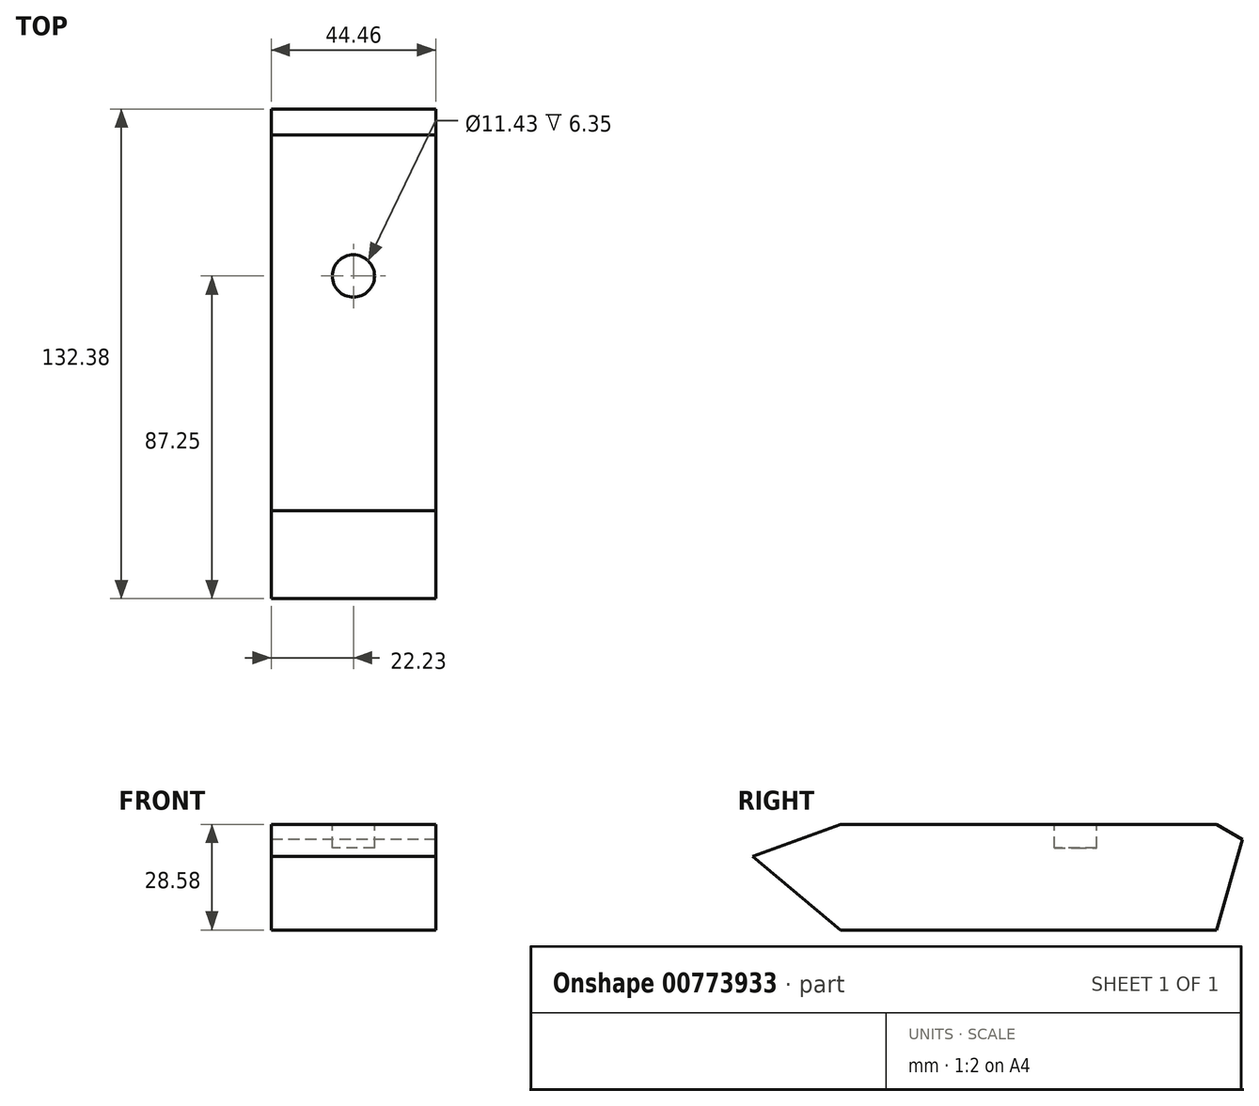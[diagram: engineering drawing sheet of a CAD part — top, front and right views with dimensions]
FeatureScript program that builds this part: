
annotation { "Feature Type Name" : "Feature", "Feature Type Description" : "" }
export const myFeature = defineFeature(function(context is Context, id is Id, definition is map)
    precondition{}
    {
        {
            var Q0;
            Q0=qCreatedBy(makeId("Right.planeOp"),FACE);
            var sketch = newSketch(context, id + "F0", { "sketchPlane" : qUnion([Q0])});
            skLineSegment(sketch, "E0.bottom", {"start": v(-50.8, 14.29) * mm, "end": v(50.8, 14.29) * mm});
            skLineSegment(sketch, "E0.top", {"start": v(-50.8, -14.29) * mm, "end": v(50.8, -14.29) * mm});
            skLineSegment(sketch, "E0.left", {"start": v(-50.8, 14.29) * mm, "end": v(-50.8, -14.29) * mm});
            skLineSegment(sketch, "E0.right", {"start": v(50.8, 14.29) * mm, "end": v(50.8, -14.29) * mm});
            skPoint(sketch, "E0.middle", {"position": v(0, 0) * mm});
            skLineSegment(sketch, "E1", {"start": v(-50.8, 14.29) * mm, "end": v(-74.55, 5.64) * mm});
            skLineSegment(sketch, "E2", {"start": v(-74.55, 5.64) * mm, "end": v(-50.8, -14.29) * mm});
            skLineSegment(sketch, "E3", {"start": v(50.8, 14.29) * mm, "end": v(57.83, 10.23) * mm});
            skLineSegment(sketch, "E4", {"start": v(50.8, -14.29) * mm, "end": v(57.83, 10.23) * mm});
            skSolve(sketch);
        }
        {
            var Q0;
            Q0 = qSketchRegion(id + "F0", true);
            extrude(context, id + "F1", {"entities" : qUnion([Q0]), "endBound" : BoundingType.SYMMETRIC, "depth" : 44.45 * mm, "offsetDistance" : 25.4 * mm});
        }
        {
            var Q0;
            Q0=makeQuery(id+"F1.opExtrude","SWEPT_FACE",FACE,{"disambiguationData":[OSD([sQuery(id+"F0.wireOp",EDGE,"E0.bottom")])]});
            var sketch = newSketch(context, id + "F2", { "sketchPlane" : qUnion([Q0])});
            skLineSegment(sketch, "E5", {"start": v(0, -50.8) * mm, "end": v(0, 12.7) * mm});
            skCircle(sketch, "E6", {"center": v(0, 12.7) * mm, "radius": 5.72 * mm});
            skSolve(sketch);
        }
        {
            var Q0;
            Q0 = qSketchRegion(id + "F2", true);
            extrude(context, id + "F3", {"entities" : qUnion([Q0]), "operationType" : NewBodyOperationType.REMOVE, "oppositeDirection" : true, "depth" : 6.35 * mm, "offsetDistance" : 25.4 * mm});
        }
    });
